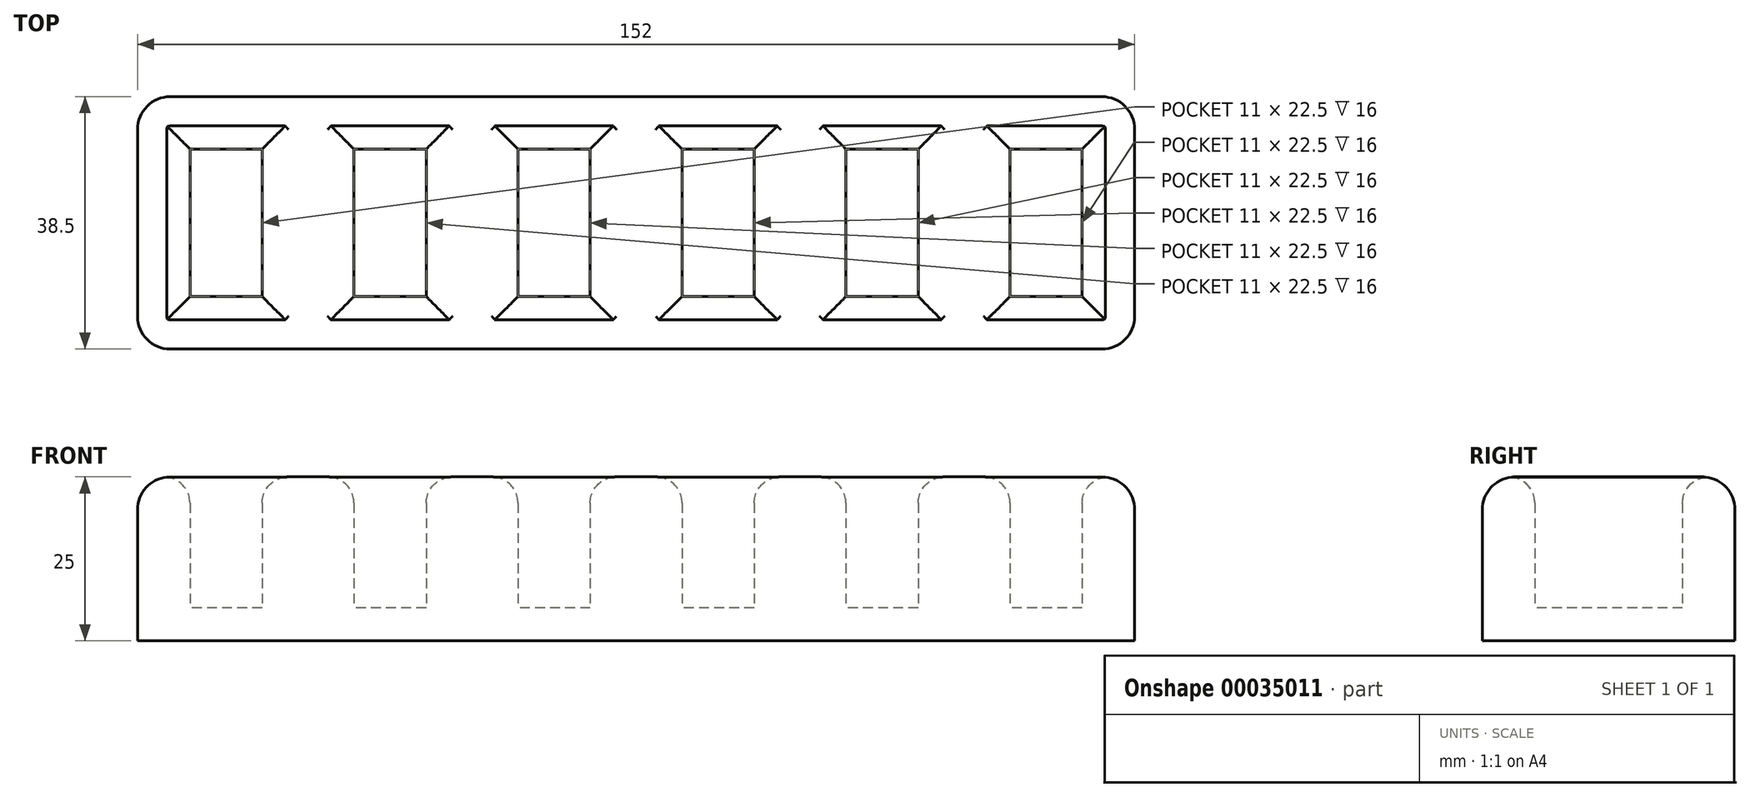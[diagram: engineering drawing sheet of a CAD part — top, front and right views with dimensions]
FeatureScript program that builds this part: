
annotation { "Feature Type Name" : "Feature", "Feature Type Description" : "" }
export const myFeature = defineFeature(function(context is Context, id is Id, definition is map)
    precondition{}
    {
        {
            var Q0;
            Q0=qCreatedBy(makeId("Top.planeOp"),FACE);
            var sketch = newSketch(context, id + "F0", { "sketchPlane" : qUnion([Q0])});
            skLineSegment(sketch, "E0.bottom", {"start": v(-85.84, 0) * mm, "end": v(-74.84, 0) * mm});
            skLineSegment(sketch, "E0.top", {"start": v(-85.84, 22.5) * mm, "end": v(-74.84, 22.5) * mm});
            skLineSegment(sketch, "E0.left", {"start": v(-85.84, 0) * mm, "end": v(-85.84, 22.5) * mm});
            skLineSegment(sketch, "E0.right", {"start": v(-74.84, 0) * mm, "end": v(-74.84, 22.5) * mm});
            skLineSegment(sketch, "E1.1.0.0", {"start": v(-60.84, 22.5) * mm, "end": v(-49.84, 22.5) * mm});
            skLineSegment(sketch, "E1.1.0.1", {"start": v(-49.84, 0) * mm, "end": v(-49.84, 22.5) * mm});
            skLineSegment(sketch, "E1.1.0.2", {"start": v(-60.84, 0) * mm, "end": v(-60.84, 22.5) * mm});
            skLineSegment(sketch, "E1.1.0.3", {"start": v(-60.84, 0) * mm, "end": v(-49.84, 0) * mm});
            skLineSegment(sketch, "E1.2.0.0", {"start": v(-35.84, 22.5) * mm, "end": v(-24.84, 22.5) * mm});
            skLineSegment(sketch, "E1.2.0.1", {"start": v(-24.84, 0) * mm, "end": v(-24.84, 22.5) * mm});
            skLineSegment(sketch, "E1.2.0.2", {"start": v(-35.84, 0) * mm, "end": v(-35.84, 22.5) * mm});
            skLineSegment(sketch, "E1.2.0.3", {"start": v(-35.84, 0) * mm, "end": v(-24.84, 0) * mm});
            skLineSegment(sketch, "E1.3.0.0", {"start": v(-10.84, 22.5) * mm, "end": v(0.16, 22.5) * mm});
            skLineSegment(sketch, "E1.3.0.1", {"start": v(0.16, 0) * mm, "end": v(0.16, 22.5) * mm});
            skLineSegment(sketch, "E1.3.0.2", {"start": v(-10.84, 0) * mm, "end": v(-10.84, 22.5) * mm});
            skLineSegment(sketch, "E1.3.0.3", {"start": v(-10.84, 0) * mm, "end": v(0.16, 0) * mm});
            skLineSegment(sketch, "E1.4.0.0", {"start": v(14.16, 22.5) * mm, "end": v(25.16, 22.5) * mm});
            skLineSegment(sketch, "E1.4.0.1", {"start": v(25.16, 0) * mm, "end": v(25.16, 22.5) * mm});
            skLineSegment(sketch, "E1.4.0.2", {"start": v(14.16, 0) * mm, "end": v(14.16, 22.5) * mm});
            skLineSegment(sketch, "E1.4.0.3", {"start": v(14.16, 0) * mm, "end": v(25.16, 0) * mm});
            skLineSegment(sketch, "E1.direction1", {"start": v(-85.84, 0) * mm, "end": v(-60.84, 0) * mm, "construction": true});
            skLineSegment(sketch, "E2", {"start": v(58.16, -8) * mm, "end": v(58.16, 30.5) * mm});
            skLineSegment(sketch, "E3", {"start": v(-85.84, 22.5) * mm, "end": v(-93.84, 22.5) * mm, "construction": true});
            skLineSegment(sketch, "E4", {"start": v(58.16, 30.5) * mm, "end": v(-93.84, 30.5) * mm});
            skLineSegment(sketch, "E5", {"start": v(-93.84, 30.5) * mm, "end": v(-93.84, -8) * mm});
            skLineSegment(sketch, "E6", {"start": v(-93.84, -8) * mm, "end": v(58.16, -8) * mm});
            skLineSegment(sketch, "E7.0.5.0", {"start": v(39.16, 22.5) * mm, "end": v(50.16, 22.5) * mm});
            skLineSegment(sketch, "E7.3.5.0", {"start": v(50.16, 0) * mm, "end": v(50.16, 22.5) * mm});
            skLineSegment(sketch, "E7.6.5.0", {"start": v(39.16, 0) * mm, "end": v(39.16, 22.5) * mm});
            skLineSegment(sketch, "E7.9.5.0", {"start": v(39.16, 0) * mm, "end": v(50.16, 0) * mm});
            skSolve(sketch);
        }
        {
            var Q0;
            Q0=makeQuery(id+"F0.imprint","IMPRINT",FACE,{"disambiguationData":[TD([[makeQuery(id+"F0.imprint","IMPRINT",EDGE,{"derivedFrom":sQuery(id+"F0.wireOp",EDGE,"E0.bottom")}),-1.0]])]});
            var Q1;
            Q1=makeQuery(id+"F0.imprint","IMPRINT",FACE,{"disambiguationData":[TD([[makeQuery(id+"F0.imprint","IMPRINT",EDGE,{"derivedFrom":sQuery(id+"F0.wireOp",EDGE,"E0.bottom")}),1.0]])]});
            var Q2;
            Q2=makeQuery(id+"F0.imprint","IMPRINT",FACE,{"disambiguationData":[TD([[makeQuery(id+"F0.imprint","IMPRINT",EDGE,{"derivedFrom":sQuery(id+"F0.wireOp",EDGE,"E1.1.0.0")}),-1.0]])]});
            var Q3;
            Q3=makeQuery(id+"F0.imprint","IMPRINT",FACE,{"disambiguationData":[TD([[makeQuery(id+"F0.imprint","IMPRINT",EDGE,{"derivedFrom":sQuery(id+"F0.wireOp",EDGE,"E1.2.0.0")}),-1.0]])]});
            var Q4;
            Q4=makeQuery(id+"F0.imprint","IMPRINT",FACE,{"disambiguationData":[TD([[makeQuery(id+"F0.imprint","IMPRINT",EDGE,{"derivedFrom":sQuery(id+"F0.wireOp",EDGE,"E1.3.0.0")}),-1.0]])]});
            var Q5;
            Q5=makeQuery(id+"F0.imprint","IMPRINT",FACE,{"disambiguationData":[TD([[makeQuery(id+"F0.imprint","IMPRINT",EDGE,{"derivedFrom":sQuery(id+"F0.wireOp",EDGE,"E1.4.0.0")}),-1.0]])]});
            var Q6;
            Q6=makeQuery(id+"F0.imprint","IMPRINT",FACE,{"disambiguationData":[TD([[makeQuery(id+"F0.imprint","IMPRINT",EDGE,{"derivedFrom":sQuery(id+"F0.wireOp",EDGE,"E7.0.5.0")}),-1.0]])]});
            extrude(context, id + "F1", {"entities" : qUnion([Q0, Q1, Q2, Q3, Q4, Q5, Q6]), "depth" : 5 * mm});
        }
        {
            var Q0;
            Q0=makeQuery(id+"F0.imprint","IMPRINT",FACE,{"disambiguationData":[TD([[makeQuery(id+"F0.imprint","IMPRINT",EDGE,{"derivedFrom":sQuery(id+"F0.wireOp",EDGE,"E0.bottom")}),-1.0]])]});
            extrude(context, id + "F2", {"entities" : qUnion([Q0]), "operationType" : NewBodyOperationType.ADD, "depth" : 25 * mm});
        }
        {
            var Q0;
            Q0=makeQuery(id+"F2.opExtrude","CAP_EDGE",EDGE,{"disambiguationData":[OSD([sQuery(id+"F0.wireOp",EDGE,"E0.left")])],"isStart":false});
            var Q1;
            Q1=makeQuery(id+"F2.opExtrude","CAP_EDGE",EDGE,{"disambiguationData":[OSD([sQuery(id+"F0.wireOp",EDGE,"E0.top")])],"isStart":false});
            var Q2;
            Q2=makeQuery(id+"F2.opExtrude","CAP_EDGE",EDGE,{"disambiguationData":[OSD([sQuery(id+"F0.wireOp",EDGE,"E0.right")])],"isStart":false});
            var Q3;
            Q3=makeQuery(id+"F2.opExtrude","CAP_EDGE",EDGE,{"disambiguationData":[OSD([sQuery(id+"F0.wireOp",EDGE,"E0.bottom")])],"isStart":false});
            var Q4;
            Q4=makeQuery(id+"F2.opExtrude","CAP_EDGE",EDGE,{"disambiguationData":[OSD([sQuery(id+"F0.wireOp",EDGE,"E1.1.0.2")])],"isStart":false});
            var Q5;
            Q5=makeQuery(id+"F2.opExtrude","CAP_EDGE",EDGE,{"disambiguationData":[OSD([sQuery(id+"F0.wireOp",EDGE,"E1.1.0.0")])],"isStart":false});
            var Q6;
            Q6=makeQuery(id+"F2.opExtrude","CAP_EDGE",EDGE,{"disambiguationData":[OSD([sQuery(id+"F0.wireOp",EDGE,"E1.1.0.1")])],"isStart":false});
            var Q7;
            Q7=makeQuery(id+"F2.opExtrude","CAP_EDGE",EDGE,{"disambiguationData":[OSD([sQuery(id+"F0.wireOp",EDGE,"E1.1.0.3")])],"isStart":false});
            var Q8;
            Q8=makeQuery(id+"F2.opExtrude","CAP_EDGE",EDGE,{"disambiguationData":[OSD([sQuery(id+"F0.wireOp",EDGE,"E1.2.0.2")])],"isStart":false});
            var Q9;
            Q9=makeQuery(id+"F2.opExtrude","CAP_EDGE",EDGE,{"disambiguationData":[OSD([sQuery(id+"F0.wireOp",EDGE,"E1.2.0.0")])],"isStart":false});
            var Q10;
            Q10=makeQuery(id+"F2.opExtrude","CAP_EDGE",EDGE,{"disambiguationData":[OSD([sQuery(id+"F0.wireOp",EDGE,"E1.2.0.1")])],"isStart":false});
            var Q11;
            Q11=makeQuery(id+"F2.opExtrude","CAP_EDGE",EDGE,{"disambiguationData":[OSD([sQuery(id+"F0.wireOp",EDGE,"E1.2.0.3")])],"isStart":false});
            var Q12;
            Q12=makeQuery(id+"F2.opExtrude","CAP_EDGE",EDGE,{"disambiguationData":[OSD([sQuery(id+"F0.wireOp",EDGE,"E1.3.0.3")])],"isStart":false});
            var Q13;
            Q13=makeQuery(id+"F2.opExtrude","CAP_EDGE",EDGE,{"disambiguationData":[OSD([sQuery(id+"F0.wireOp",EDGE,"E1.3.0.2")])],"isStart":false});
            var Q14;
            Q14=makeQuery(id+"F2.opExtrude","CAP_EDGE",EDGE,{"disambiguationData":[OSD([sQuery(id+"F0.wireOp",EDGE,"E1.3.0.0")])],"isStart":false});
            var Q15;
            Q15=makeQuery(id+"F2.opExtrude","CAP_EDGE",EDGE,{"disambiguationData":[OSD([sQuery(id+"F0.wireOp",EDGE,"E1.3.0.1")])],"isStart":false});
            var Q16;
            Q16=makeQuery(id+"F2.opExtrude","CAP_EDGE",EDGE,{"disambiguationData":[OSD([sQuery(id+"F0.wireOp",EDGE,"E1.4.0.0")])],"isStart":false});
            var Q17;
            Q17=makeQuery(id+"F2.opExtrude","CAP_EDGE",EDGE,{"disambiguationData":[OSD([sQuery(id+"F0.wireOp",EDGE,"E1.4.0.2")])],"isStart":false});
            var Q18;
            Q18=makeQuery(id+"F2.opExtrude","CAP_EDGE",EDGE,{"disambiguationData":[OSD([sQuery(id+"F0.wireOp",EDGE,"E1.4.0.1")])],"isStart":false});
            var Q19;
            Q19=makeQuery(id+"F2.opExtrude","CAP_EDGE",EDGE,{"disambiguationData":[OSD([sQuery(id+"F0.wireOp",EDGE,"E1.4.0.3")])],"isStart":false});
            var Q20;
            Q20=makeQuery(id+"F2.opExtrude","CAP_EDGE",EDGE,{"disambiguationData":[OSD([sQuery(id+"F0.wireOp",EDGE,"E7.0.5.0")])],"isStart":false});
            var Q21;
            Q21=makeQuery(id+"F2.opExtrude","CAP_EDGE",EDGE,{"disambiguationData":[OSD([sQuery(id+"F0.wireOp",EDGE,"E7.3.5.0")])],"isStart":false});
            var Q22;
            Q22=makeQuery(id+"F2.opExtrude","CAP_EDGE",EDGE,{"disambiguationData":[OSD([sQuery(id+"F0.wireOp",EDGE,"E7.6.5.0")])],"isStart":false});
            var Q23;
            Q23=makeQuery(id+"F2.opExtrude","CAP_EDGE",EDGE,{"disambiguationData":[OSD([sQuery(id+"F0.wireOp",EDGE,"E7.9.5.0")])],"isStart":false});
            fillet(context, id + "F3", {"entities" : qUnion([Q0, Q1, Q2, Q3, Q4, Q5, Q6, Q7, Q8, Q9, Q10, Q11, Q12, Q13, Q14, Q15, Q16, Q17, Q18, Q19, Q20, Q21, Q22, Q23]), "radius" : 4 * mm, "tangentPropagation" : true, "allowEdgeOverflow" : false});
        }
        {
            var Q0;
            Q0=makeQuery(id+"F2.opExtrude","CAP_EDGE",EDGE,{"disambiguationData":[OSD([sQuery(id+"F0.wireOp",EDGE,"E6")])],"isStart":false});
            var Q1;
            Q1=makeQuery(id+"F2.opExtrude","CAP_EDGE",EDGE,{"disambiguationData":[OSD([sQuery(id+"F0.wireOp",EDGE,"E5")])],"isStart":false});
            var Q2;
            Q2=makeQuery(id+"F2.opExtrude","CAP_EDGE",EDGE,{"disambiguationData":[OSD([sQuery(id+"F0.wireOp",EDGE,"E4")])],"isStart":false});
            var Q3;
            Q3=makeQuery(id+"F2.opExtrude","CAP_EDGE",EDGE,{"disambiguationData":[OSD([sQuery(id+"F0.wireOp",EDGE,"E2")])],"isStart":false});
            fillet(context, id + "F4", {"entities" : qUnion([Q0, Q1, Q2, Q3]), "radius" : 5 * mm, "tangentPropagation" : true, "allowEdgeOverflow" : false});
        }
        {
            var Q0;
            {var subQ0=sQuery(id+"F0.wireOp",EDGE,"E6");var subQ1=sQuery(id+"F0.wireOp",EDGE,"E5");Q0=makeQuery(id+"F2.boolean.opBoolean","MERGE",EDGE,{"derivedFrom":[makeQuery(id+"F1.opExtrude","SWEPT_EDGE",EDGE,{"disambiguationData":[OSD([subQ1,subQ0])]}),makeQuery(id+"F2.opExtrude","SWEPT_EDGE",EDGE,{"disambiguationData":[OSD([subQ1,subQ0])]})]});}
            var Q1;
            {var subQ0=sQuery(id+"F0.wireOp",EDGE,"E6");var subQ1=sQuery(id+"F0.wireOp",EDGE,"E2");Q1=makeQuery(id+"F2.boolean.opBoolean","MERGE",EDGE,{"derivedFrom":[makeQuery(id+"F1.opExtrude","SWEPT_EDGE",EDGE,{"disambiguationData":[OSD([subQ1,subQ0])]}),makeQuery(id+"F2.opExtrude","SWEPT_EDGE",EDGE,{"disambiguationData":[OSD([subQ1,subQ0])]})]});}
            var Q2;
            {var subQ0=sQuery(id+"F0.wireOp",EDGE,"E4");var subQ1=sQuery(id+"F0.wireOp",EDGE,"E2");Q2=makeQuery(id+"F2.boolean.opBoolean","MERGE",EDGE,{"derivedFrom":[makeQuery(id+"F1.opExtrude","SWEPT_EDGE",EDGE,{"disambiguationData":[OSD([subQ1,subQ0])]}),makeQuery(id+"F2.opExtrude","SWEPT_EDGE",EDGE,{"disambiguationData":[OSD([subQ1,subQ0])]})]});}
            var Q3;
            {var subQ0=sQuery(id+"F0.wireOp",EDGE,"E5");var subQ1=sQuery(id+"F0.wireOp",EDGE,"E4");Q3=makeQuery(id+"F2.boolean.opBoolean","MERGE",EDGE,{"derivedFrom":[makeQuery(id+"F1.opExtrude","SWEPT_EDGE",EDGE,{"disambiguationData":[OSD([subQ1,subQ0])]}),makeQuery(id+"F2.opExtrude","SWEPT_EDGE",EDGE,{"disambiguationData":[OSD([subQ1,subQ0])]})]});}
            fillet(context, id + "F5", {"entities" : qUnion([Q0, Q1, Q2, Q3]), "radius" : 5 * mm, "tangentPropagation" : true, "allowEdgeOverflow" : false});
        }
    });
